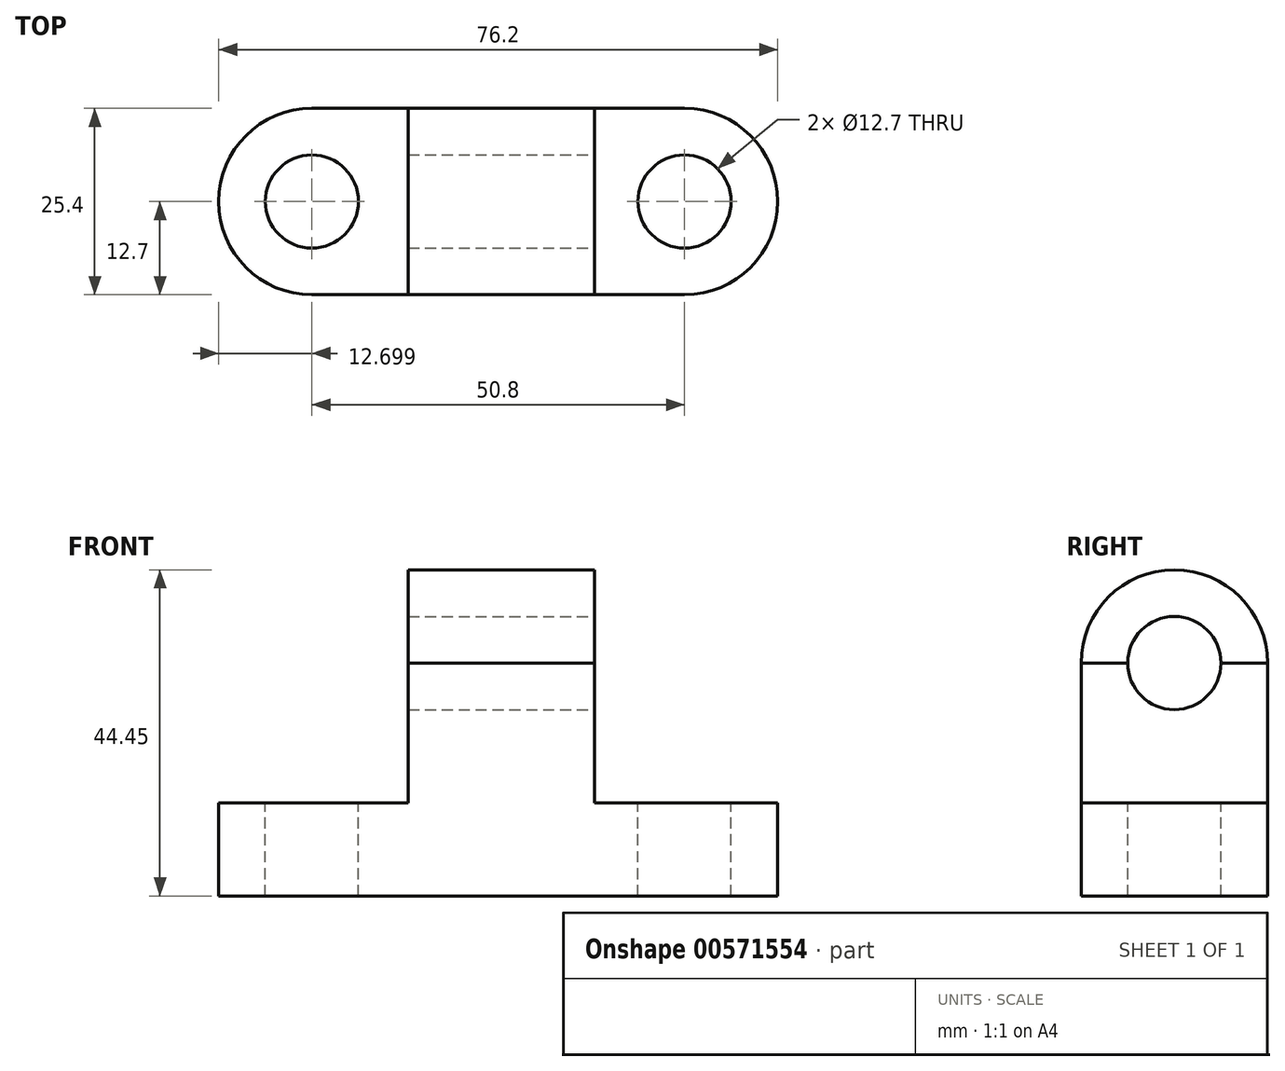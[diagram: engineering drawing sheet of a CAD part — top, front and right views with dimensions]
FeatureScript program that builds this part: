
annotation { "Feature Type Name" : "Feature", "Feature Type Description" : "" }
export const myFeature = defineFeature(function(context is Context, id is Id, definition is map)
    precondition{}
    {
        {
            var Q0;
            Q0=qCreatedBy(makeId("Front.planeOp"),FACE);
            var sketch = newSketch(context, id + "F0", { "sketchPlane" : qUnion([Q0])});
            skLineSegment(sketch, "E0", {"start": v(-44.31, 44.6) * mm, "end": v(-18.91, 44.6) * mm});
            skLineSegment(sketch, "E1", {"start": v(-18.91, 44.6) * mm, "end": v(-18.91, 25.55) * mm});
            skLineSegment(sketch, "E2", {"start": v(-18.91, 25.55) * mm, "end": v(-6.64, 25.55) * mm});
            skLineSegment(sketch, "E3", {"start": v(-6.64, 25.55) * mm, "end": v(-6.64, 12.85) * mm});
            skLineSegment(sketch, "E4", {"start": v(-6.64, 12.85) * mm, "end": v(-57.44, 12.85) * mm});
            skLineSegment(sketch, "E5", {"start": v(-57.44, 12.85) * mm, "end": v(-57.44, 25.55) * mm});
            skLineSegment(sketch, "E6", {"start": v(-57.44, 25.55) * mm, "end": v(-44.31, 25.55) * mm});
            skLineSegment(sketch, "E7", {"start": v(-44.31, 25.55) * mm, "end": v(-44.31, 44.6) * mm});
            skSolve(sketch);
        }
        {
            var Q0;
            Q0=makeQuery(id+"F0.imprint","IMPRINT",FACE,{"disambiguationData":[TD([[makeQuery(id+"F0.imprint","IMPRINT",EDGE,{"derivedFrom":sQuery(id+"F0.wireOp",EDGE,"E0")}),-1.0]])]});
            extrude(context, id + "F1", {"entities" : qUnion([Q0]), "depth" : 25.4 * mm, "offsetDistance" : 25.4 * mm});
        }
        {
            var Q0;
            Q0=makeQuery(id+"F1.opExtrude","SWEPT_FACE",FACE,{"disambiguationData":[OSD([sQuery(id+"F0.wireOp",EDGE,"E2")])]});
            var sketch = newSketch(context, id + "F2", { "sketchPlane" : qUnion([Q0])});
            skArc(sketch, "E8", {"start": v(-6.64, -25.4) * mm, "mid": v(6.06, -12.7) * mm, "end": v(-6.64, 0) * mm});
            skSolve(sketch);
        }
        {
            var Q0;
            Q0=makeQuery(id+"F1.opExtrude","SWEPT_FACE",FACE,{"disambiguationData":[OSD([sQuery(id+"F0.wireOp",EDGE,"E6")])]});
            var sketch = newSketch(context, id + "F3", { "sketchPlane" : qUnion([Q0])});
            skArc(sketch, "E9", {"start": v(-57.44, 0) * mm, "mid": v(-70.14, -12.7) * mm, "end": v(-57.44, -25.4) * mm});
            skSolve(sketch);
        }
        {
            var Q0;
            Q0=makeQuery(id+"F3.imprint","IMPRINT",FACE,{"disambiguationData":[TD([[makeQuery(id+"F3.imprint","IMPRINT",EDGE,{"derivedFrom":sQuery(id+"F3.wireOp",EDGE,"E9")}),1.0]])]});
            var Q1;
            Q1=makeQuery(id+"F2.imprint","IMPRINT",FACE,{"disambiguationData":[TD([[makeQuery(id+"F2.imprint","IMPRINT",EDGE,{"derivedFrom":sQuery(id+"F2.wireOp",EDGE,"E8")}),1.0]])]});
            extrude(context, id + "F4", {"entities" : qUnion([Q0, Q1]), "operationType" : NewBodyOperationType.ADD, "oppositeDirection" : true, "depth" : 12.7 * mm, "offsetDistance" : 25.4 * mm});
        }
        {
            var Q0;
            Q0=makeQuery(id+"F1.opExtrude","SWEPT_FACE",FACE,{"disambiguationData":[OSD([sQuery(id+"F0.wireOp",EDGE,"E1")])]});
            var sketch = newSketch(context, id + "F5", { "sketchPlane" : qUnion([Q0])});
            skArc(sketch, "E10", {"start": v(0, 44.6) * mm, "mid": v(-12.7, 57.3) * mm, "end": v(-25.4, 44.6) * mm});
            skSolve(sketch);
        }
        {
            var Q0;
            Q0=makeQuery(id+"F5.imprint","IMPRINT",FACE,{"disambiguationData":[TD([[makeQuery(id+"F5.imprint","IMPRINT",EDGE,{"derivedFrom":sQuery(id+"F5.wireOp",EDGE,"E10")}),1.0]])]});
            extrude(context, id + "F6", {"entities" : qUnion([Q0]), "oppositeDirection" : true, "depth" : 25.4 * mm, "offsetDistance" : 25.4 * mm});
        }
        {
            var Q0;
            {var subQ0=sQuery(id+"F0.wireOp",EDGE,"E6");Q0=makeQuery(id+"F4.boolean.opBoolean","MERGE",FACE,{"derivedFrom":[makeQuery(id+"F1.opExtrude","SWEPT_FACE",FACE,{"disambiguationData":[OSD([subQ0])]}),makeQuery(id+"F4.opExtrude","CAP_FACE",FACE,{"disambiguationData":[OSD([sQuery(id+"F0.wireOp",EDGE,"E5"),subQ0,sQuery(id+"F3.wireOp",EDGE,"E9")])],"isStart":true})]});}
            var sketch = newSketch(context, id + "F7", { "sketchPlane" : qUnion([Q0])});
            skCircle(sketch, "E11", {"center": v(-57.44, -12.7) * mm, "radius": 6.35 * mm});
            skSolve(sketch);
        }
        {
            var Q0;
            Q0=sQuery(id+"F7.wireOp",VERTEX,"E11.center");
            var Q1;
            Q1=makeQuery(id+"F1.opExtrude","SWEPT_BODY",BODY,{"disambiguationData":[OSD([sQuery(id+"F0.wireOp",EDGE,"E0"),sQuery(id+"F0.wireOp",EDGE,"E1"),sQuery(id+"F0.wireOp",EDGE,"E2"),sQuery(id+"F0.wireOp",EDGE,"E3"),sQuery(id+"F0.wireOp",EDGE,"E4"),sQuery(id+"F0.wireOp",EDGE,"E5"),sQuery(id+"F0.wireOp",EDGE,"E6"),sQuery(id+"F0.wireOp",EDGE,"E7")])]});
            hole(context, id + "F8", {"style" : HoleStyle.SIMPLE, "endStyle" : HoleEndStyle.THROUGH, "holeDiameter" : 12.7 * mm, "isTappedThrough" : true, "tappedDepth" : 12.7 * mm, "tapClearance" : 3, "locations" : qUnion([Q0]), "scope" : qUnion([Q1])});
        }
        {
            var Q0;
            {var subQ0=sQuery(id+"F0.wireOp",EDGE,"E2");Q0=makeQuery(id+"F4.boolean.opBoolean","MERGE",FACE,{"derivedFrom":[makeQuery(id+"F1.opExtrude","SWEPT_FACE",FACE,{"disambiguationData":[OSD([subQ0])]}),makeQuery(id+"F4.opExtrude","CAP_FACE",FACE,{"disambiguationData":[OSD([subQ0,sQuery(id+"F0.wireOp",EDGE,"E3"),sQuery(id+"F2.wireOp",EDGE,"E8")])],"isStart":true})]});}
            var sketch = newSketch(context, id + "F9", { "sketchPlane" : qUnion([Q0])});
            skCircle(sketch, "E12", {"center": v(-6.64, -12.7) * mm, "radius": 6.35 * mm});
            skSolve(sketch);
        }
        {
            var Q0;
            Q0=sQuery(id+"F9.wireOp",VERTEX,"E12.center");
            var Q1;
            Q1=makeQuery(id+"F1.opExtrude","SWEPT_BODY",BODY,{"disambiguationData":[OSD([sQuery(id+"F0.wireOp",EDGE,"E0"),sQuery(id+"F0.wireOp",EDGE,"E1"),sQuery(id+"F0.wireOp",EDGE,"E2"),sQuery(id+"F0.wireOp",EDGE,"E3"),sQuery(id+"F0.wireOp",EDGE,"E4"),sQuery(id+"F0.wireOp",EDGE,"E5"),sQuery(id+"F0.wireOp",EDGE,"E6"),sQuery(id+"F0.wireOp",EDGE,"E7")])]});
            hole(context, id + "F10", {"style" : HoleStyle.SIMPLE, "endStyle" : HoleEndStyle.THROUGH, "holeDiameter" : 12.7 * mm, "isTappedThrough" : true, "tappedDepth" : 12.7 * mm, "tapClearance" : 3, "locations" : qUnion([Q0]), "scope" : qUnion([Q1])});
        }
        {
            var Q0;
            Q0=makeQuery(id+"F1.opExtrude","SWEPT_FACE",FACE,{"disambiguationData":[OSD([sQuery(id+"F0.wireOp",EDGE,"E1")])]});
            var sketch = newSketch(context, id + "F11", { "sketchPlane" : qUnion([Q0])});
            skCircle(sketch, "E13", {"center": v(-12.7, 44.6) * mm, "radius": 6.35 * mm});
            skSolve(sketch);
        }
        {
            var Q0;
            Q0=sQuery(id+"F11.wireOp",VERTEX,"E13.center");
            var Q1;
            Q1=makeQuery(id+"F1.opExtrude","SWEPT_BODY",BODY,{"disambiguationData":[OSD([sQuery(id+"F0.wireOp",EDGE,"E0"),sQuery(id+"F0.wireOp",EDGE,"E1"),sQuery(id+"F0.wireOp",EDGE,"E2"),sQuery(id+"F0.wireOp",EDGE,"E3"),sQuery(id+"F0.wireOp",EDGE,"E4"),sQuery(id+"F0.wireOp",EDGE,"E5"),sQuery(id+"F0.wireOp",EDGE,"E6"),sQuery(id+"F0.wireOp",EDGE,"E7")])]});
            var Q2;
            Q2=makeQuery(id+"F6.opExtrude","SWEPT_BODY",BODY,{"disambiguationData":[OSD([sQuery(id+"F0.wireOp",EDGE,"E0"),sQuery(id+"F0.wireOp",EDGE,"E1"),sQuery(id+"F5.wireOp",EDGE,"E10")])]});
            hole(context, id + "F12", {"style" : HoleStyle.SIMPLE, "endStyle" : HoleEndStyle.THROUGH, "holeDiameter" : 12.7 * mm, "isTappedThrough" : true, "tappedDepth" : 12.7 * mm, "tapClearance" : 3, "locations" : qUnion([Q0]), "scope" : qUnion([Q1, Q2])});
        }
    });
